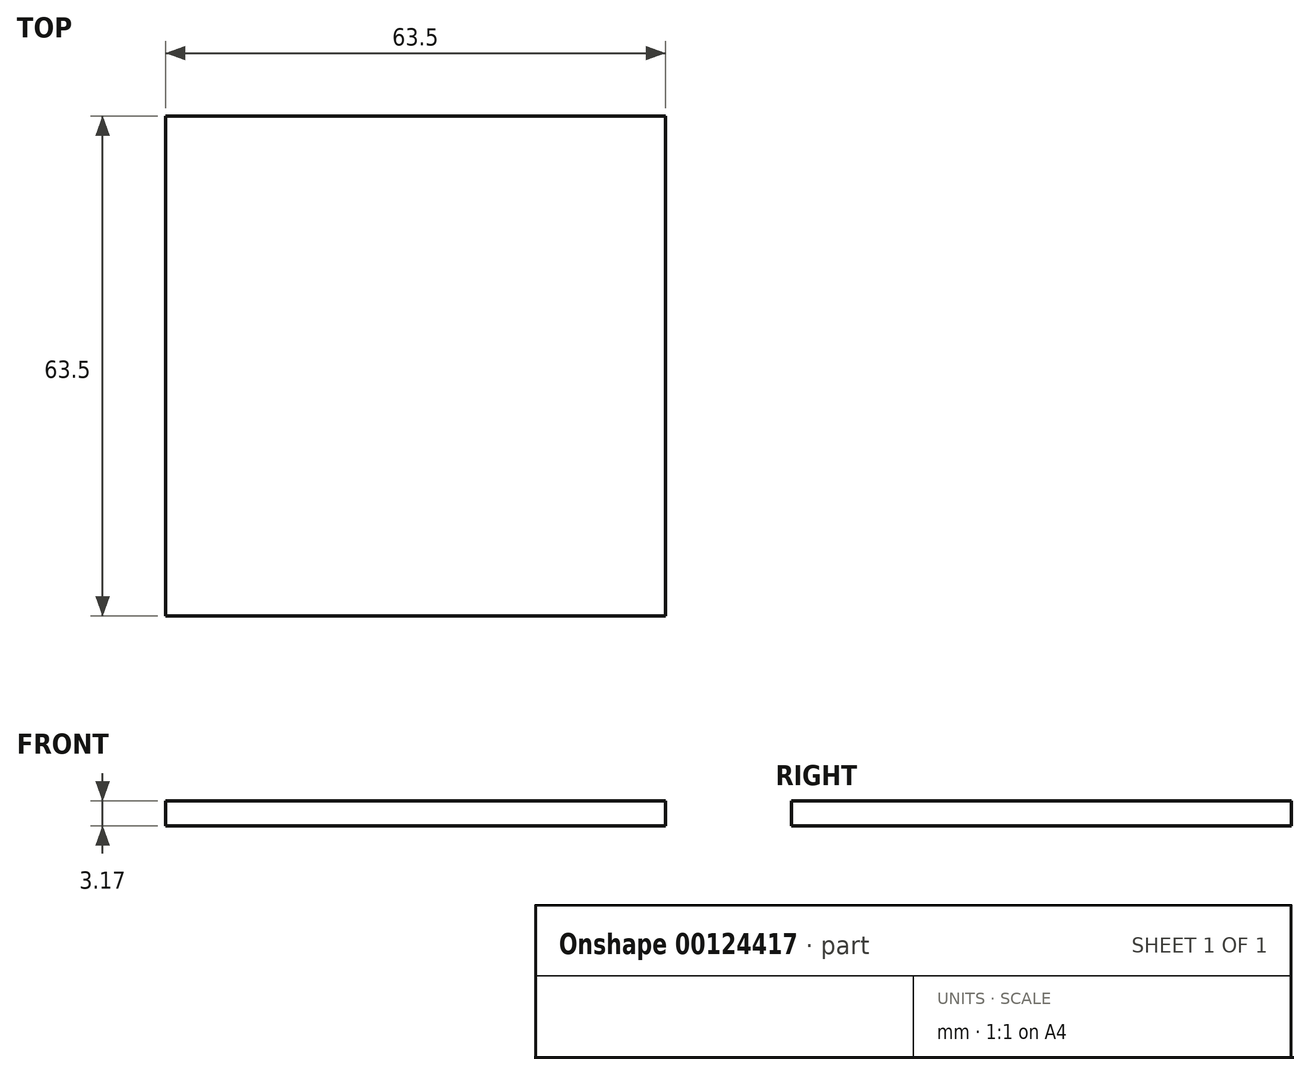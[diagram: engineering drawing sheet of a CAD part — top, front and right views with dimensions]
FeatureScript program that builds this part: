
annotation { "Feature Type Name" : "Feature", "Feature Type Description" : "" }
export const myFeature = defineFeature(function(context is Context, id is Id, definition is map)
    precondition{}
    {
        {
            var Q0;
            Q0=qCreatedBy(makeId("Top.planeOp"),FACE);
            var sketch = newSketch(context, id + "F0", { "sketchPlane" : qUnion([Q0])});
            skLineSegment(sketch, "E0.bottom", {"start": v(31.75, -31.75) * mm, "end": v(-31.75, -31.75) * mm});
            skLineSegment(sketch, "E0.top", {"start": v(31.75, 31.75) * mm, "end": v(-31.75, 31.75) * mm});
            skLineSegment(sketch, "E0.left", {"start": v(31.75, -31.75) * mm, "end": v(31.75, 31.75) * mm});
            skLineSegment(sketch, "E0.right", {"start": v(-31.75, -31.75) * mm, "end": v(-31.75, 31.75) * mm});
            skPoint(sketch, "E0.middle", {"position": v(0, 0) * mm});
            skSolve(sketch);
        }
        {
            var Q0;
            Q0=makeQuery(id+"F0.imprint","IMPRINT",FACE,{"disambiguationData":[TD([[makeQuery(id+"F0.imprint","IMPRINT",EDGE,{"derivedFrom":sQuery(id+"F0.wireOp",EDGE,"E0.bottom")}),-1.0]])]});
            extrude(context, id + "F1", {"entities" : qUnion([Q0]), "depth" : 3.17 * mm});
        }
    });
